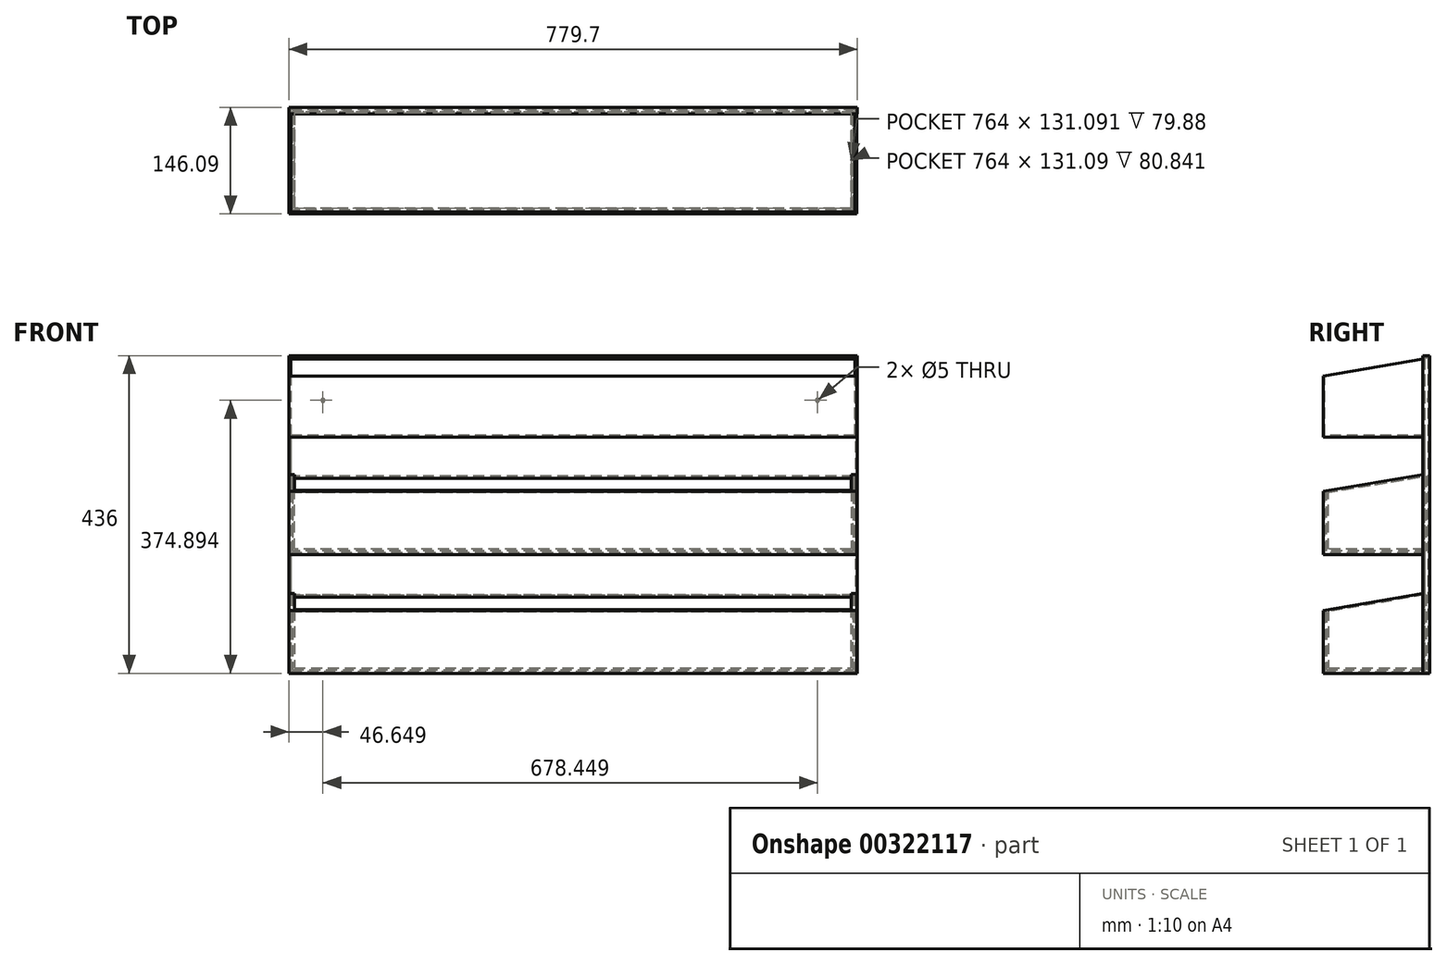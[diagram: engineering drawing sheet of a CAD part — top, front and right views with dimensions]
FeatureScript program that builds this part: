
annotation { "Feature Type Name" : "Feature", "Feature Type Description" : "" }
export const myFeature = defineFeature(function(context is Context, id is Id, definition is map)
    precondition{}
    {
        {
            var Q0;
            Q0=qCreatedBy(makeId("Front.planeOp"),FACE);
            var sketch = newSketch(context, id + "F0", { "sketchPlane" : qUnion([Q0])});
            skLineSegment(sketch, "E0.bottom", {"start": v(-387.35, 215.5) * mm, "end": v(387.35, 215.5) * mm});
            skLineSegment(sketch, "E0.top", {"start": v(-387.35, -215.5) * mm, "end": v(387.35, -215.5) * mm});
            skLineSegment(sketch, "E0.left", {"start": v(-387.35, 215.5) * mm, "end": v(-387.35, -215.5) * mm});
            skLineSegment(sketch, "E0.right", {"start": v(387.35, 215.5) * mm, "end": v(387.35, -215.5) * mm});
            skPoint(sketch, "E0.middle", {"position": v(0, 0) * mm});
            skSolve(sketch);
        }
        {
            var Q0;
            Q0 = qSketchRegion(id + "F0", true);
            var Q1;
            Q1=makeQuery(id+"F0.imprint","IMPRINT",FACE,{"disambiguationData":[TD([[makeQuery(id+"F0.imprint","IMPRINT",EDGE,{"derivedFrom":sQuery(id+"F0.wireOp",EDGE,"E0.bottom")}),-1.0]])]});
            extrude(context, id + "F1", {"entities" : qUnion([Q0, Q1]), "depth" : 4 * mm});
        }
        {
            var Q0;
            Q0=makeQuery(id+"F1.opExtrude","SWEPT_FACE",FACE,{"disambiguationData":[OSD([sQuery(id+"F0.wireOp",EDGE,"E0.left")])]});
            var sketch = newSketch(context, id + "F2", { "sketchPlane" : qUnion([Q0])});
            skLineSegment(sketch, "E1", {"start": v(4, -110.47) * mm, "end": v(141.1, -134.02) * mm});
            skLineSegment(sketch, "E2", {"start": v(141.1, -134.02) * mm, "end": v(141.1, -215.5) * mm});
            skLineSegment(sketch, "E3", {"start": v(141.1, -215.5) * mm, "end": v(4, -215.5) * mm});
            skSolve(sketch);
        }
        {
            var Q0;
            Q0 = qSketchRegion(id + "F2", true);
            var Q1;
            {var subQ0=sQuery(id+"F2.wireOp",EDGE,"E1");Q1=makeQuery(id+"F2.imprint","IMPRINT",FACE,{"disambiguationData":[TD([[makeQuery(id+"F2.imprint","IMPRINT",EDGE,{"derivedFrom":subQ0}),-1.0]])]});}
            extrude(context, id + "F3", {"entities" : qUnion([Q0, Q1]), "operationType" : NewBodyOperationType.ADD, "oppositeDirection" : true, "depth" : 774 * mm});
        }
        {
            var Q0;
            Q0=makeQuery(id+"F3.opExtrude","SWEPT_FACE",FACE,{"disambiguationData":[OSD([sQuery(id+"F2.wireOp",EDGE,"E1")])]});
            shell(context, id + "F4", {"entities" : qUnion([Q0]), "thickness" : 2.5 * mm});
        }
        {
            var Q0;
            {var subQ0=sQuery(id+"F2.wireOp",EDGE,"E2");var subQ1=sQuery(id+"F0.wireOp",EDGE,"E0.left");Q0=makeQuery(id+"FKUl1M2sgUvv7a4_1.boolean.opBoolean","MERGE",FACE,{"derivedFrom":[makeQuery(id+"F3.boolean.opBoolean","MERGE",FACE,{"derivedFrom":[makeQuery(id+"F1.opExtrude","SWEPT_FACE",FACE,{"disambiguationData":[OSD([subQ1])]}),makeQuery(id+"F3.opExtrude","CAP_FACE",FACE,{"disambiguationData":[OSD([subQ1,sQuery(id+"F2.wireOp",EDGE,"E1"),subQ0,sQuery(id+"F2.wireOp",EDGE,"E3")])],"isStart":true})]}),makeQuery(id+"FKUl1M2sgUvv7a4_1.opThicken","SWEPT_FACE",FACE,{"disambiguationData":[OSD([subQ0])]})]});}
            var sketch = newSketch(context, id + "F5", { "sketchPlane" : qUnion([Q0])});
            skLineSegment(sketch, "E4", {"start": v(4, -52.52) * mm, "end": v(4, 52.52) * mm});
            skLineSegment(sketch, "E5", {"start": v(4, -52.52) * mm, "end": v(141.1, -52.52) * mm});
            skLineSegment(sketch, "E6", {"start": v(141.1, -52.52) * mm, "end": v(141.1, 29.97) * mm});
            skLineSegment(sketch, "E7", {"start": v(141.1, 29.97) * mm, "end": v(4, 52.52) * mm});
            skSolve(sketch);
        }
        {
            var Q0;
            Q0=makeQuery(id+"F5.imprint","IMPRINT",FACE,{"disambiguationData":[TD([[makeQuery(id+"F5.imprint","IMPRINT",EDGE,{"derivedFrom":sQuery(id+"F5.wireOp",EDGE,"E4")}),1.0]])]});
            extrude(context, id + "F6", {"entities" : qUnion([Q0]), "operationType" : NewBodyOperationType.ADD, "oppositeDirection" : true, "depth" : 774 * mm});
        }
        {
            var Q0;
            Q0=makeQuery(id+"F6.opExtrude","SWEPT_FACE",FACE,{"disambiguationData":[OSD([sQuery(id+"F5.wireOp",EDGE,"E7")])]});
            shell(context, id + "F7", {"entities" : qUnion([Q0]), "thickness" : 2.5 * mm});
        }
        {
            var Q0;
            {var subQ3=sQuery(id+"F5.wireOp",EDGE,"E4");Q0=makeQuery(id+"F5.imprint","IMPRINT",FACE,{"disambiguationData":[TD([[makeQuery(id+"F5.imprint","IMPRINT",EDGE,{"derivedFrom":subQ3}),-1.0]])]});}
            var sketch = newSketch(context, id + "F8", { "sketchPlane" : qUnion([Q0])});
            skLineSegment(sketch, "E8", {"start": v(4, 108.8) * mm, "end": v(4, 213.83) * mm});
            skLineSegment(sketch, "E9", {"start": v(4, 108.8) * mm, "end": v(141.1, 108.8) * mm});
            skLineSegment(sketch, "E10", {"start": v(141.1, 108.8) * mm, "end": v(141.1, 190.28) * mm});
            skLineSegment(sketch, "E11", {"start": v(141.1, 190.28) * mm, "end": v(4, 213.83) * mm});
            skSolve(sketch);
        }
        {
            var Q0;
            Q0 = qSketchRegion(id + "F8", true);
            extrude(context, id + "F9", {"entities" : qUnion([Q0]), "operationType" : NewBodyOperationType.ADD, "oppositeDirection" : true, "depth" : 774 * mm});
        }
        {
            var Q0;
            Q0=makeQuery(id+"F9.opExtrude","SWEPT_FACE",FACE,{"disambiguationData":[OSD([sQuery(id+"F8.wireOp",EDGE,"E11")])]});
            shell(context, id + "F10", {"entities" : qUnion([Q0]), "thickness" : 2.5 * mm, "oppositeDirection" : true});
        }
        {
            var Q0;
            {var subQ0=sQuery(id+"F0.wireOp",EDGE,"E0.right");var subQ1=sQuery(id+"F0.wireOp",EDGE,"E0.left");var subQ2=sQuery(id+"F0.wireOp",EDGE,"E0.top");var subQ3=sQuery(id+"F0.wireOp",EDGE,"E0.bottom");Q0=makeQuery(id+"F10.opShell","OFFSET_FACE",FACE,{"disambiguationData":[OSD([subQ3,subQ2,subQ1,subQ0]),TDD([makeQuery(id+"F1.opExtrude","CAP_FACE",FACE,{"disambiguationData":[OSD([subQ3,subQ2,subQ1,subQ0])],"isStart":true})])]});}
            var sketch = newSketch(context, id + "F11", { "sketchPlane" : qUnion([Q0])});
            skCircle(sketch, "E12", {"center": v(-343.2, 156.9) * mm, "radius": 9.75 * mm});
            skCircle(sketch, "E13", {"center": v(335.25, 156.9) * mm, "radius": 9.75 * mm});
            skSolve(sketch);
        }
        {
            var Q0;
            Q0=sQuery(id+"F11.wireOp",VERTEX,"E12.center");
            var Q1;
            Q1=makeQuery(id+"F1.opExtrude","SWEPT_BODY",BODY,{"disambiguationData":[OSD([sQuery(id+"F0.wireOp",EDGE,"E0.bottom"),sQuery(id+"F0.wireOp",EDGE,"E0.top"),sQuery(id+"F0.wireOp",EDGE,"E0.left"),sQuery(id+"F0.wireOp",EDGE,"E0.right")])]});
            hole(context, id + "F12", {"style" : HoleStyle.SIMPLE, "endStyle" : HoleEndStyle.THROUGH, "holeDiameter" : 5 * mm, "tappedDepth" : 12 * mm, "tapClearance" : 3, "locations" : qUnion([Q0]), "scope" : qUnion([Q1])});
        }
        {
            var Q0;
            Q0=sQuery(id+"F11.wireOp",VERTEX,"E13.center");
            var Q1;
            Q1=makeQuery(id+"F1.opExtrude","SWEPT_BODY",BODY,{"disambiguationData":[OSD([sQuery(id+"F0.wireOp",EDGE,"E0.bottom"),sQuery(id+"F0.wireOp",EDGE,"E0.top"),sQuery(id+"F0.wireOp",EDGE,"E0.left"),sQuery(id+"F0.wireOp",EDGE,"E0.right")])]});
            hole(context, id + "F13", {"style" : HoleStyle.SIMPLE, "endStyle" : HoleEndStyle.THROUGH, "holeDiameter" : 5 * mm, "tappedDepth" : 12 * mm, "tapClearance" : 3, "locations" : qUnion([Q0]), "scope" : qUnion([Q1])});
        }
    });
